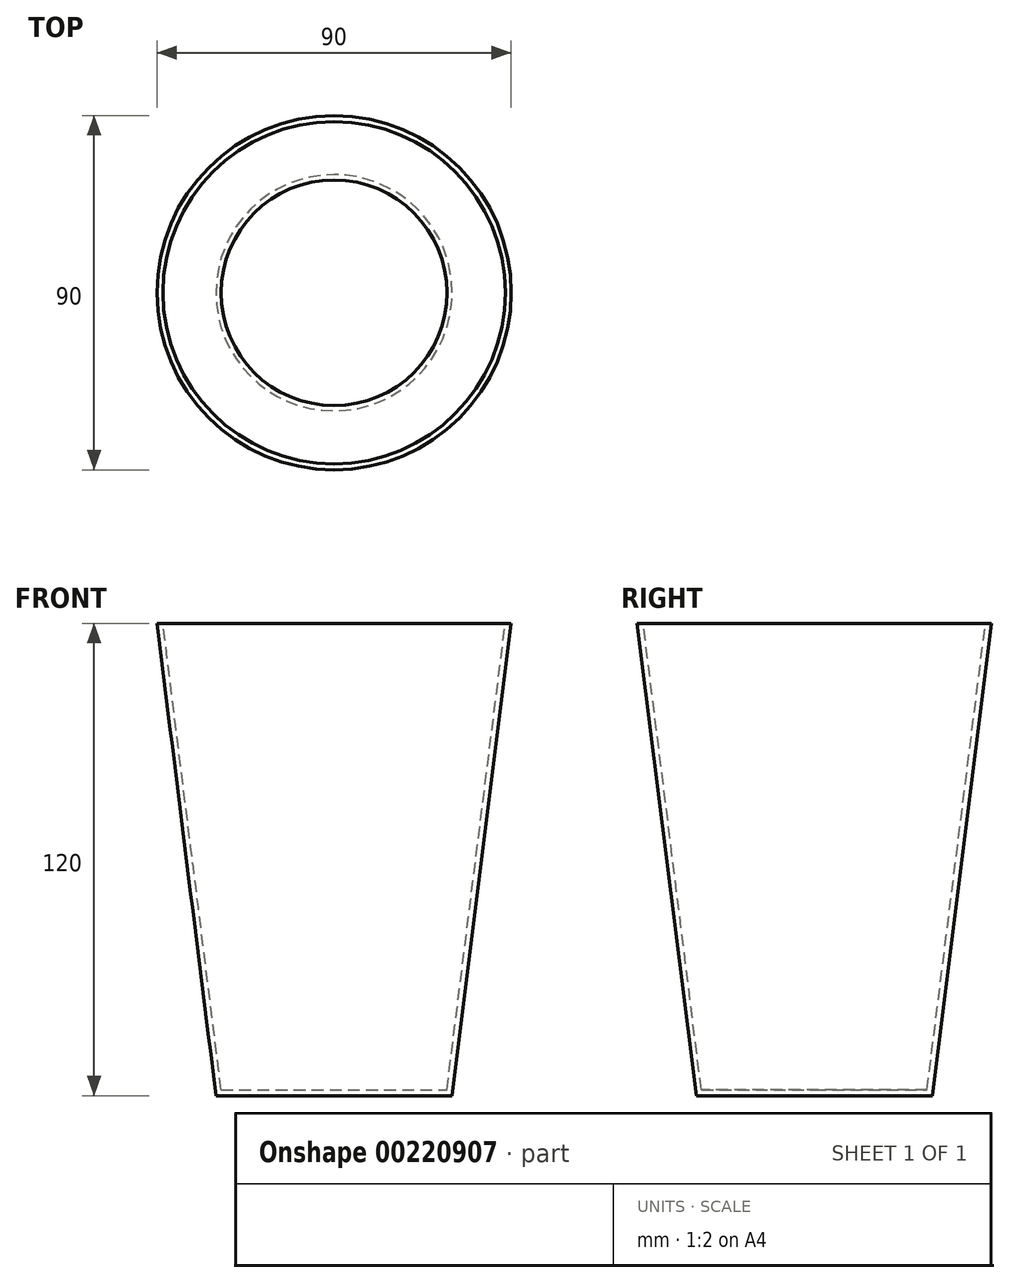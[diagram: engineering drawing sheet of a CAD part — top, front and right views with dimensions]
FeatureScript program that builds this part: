
annotation { "Feature Type Name" : "Feature", "Feature Type Description" : "" }
export const myFeature = defineFeature(function(context is Context, id is Id, definition is map)
    precondition{}
    {
        {
            var Q0;
            Q0=qCreatedBy(makeId("Top.planeOp"),FACE);
            var sketch = newSketch(context, id + "F0", { "sketchPlane" : qUnion([Q0])});
            skCircle(sketch, "E0", {"center": v(0, 0) * mm, "radius": 30 * mm});
            skSolve(sketch);
        }
        {
            var Q0;
            Q0=qCreatedBy(makeId("Front.planeOp"),FACE);
            var sketch = newSketch(context, id + "F1", { "sketchPlane" : qUnion([Q0])});
            skLineSegment(sketch, "E1", {"start": v(0, 0) * mm, "end": v(0, 120) * mm});
            skLineSegment(sketch, "E2", {"start": v(0, 0) * mm, "end": v(30, 0) * mm});
            skPoint(sketch, "E3.orphan", {"position": v(-30, 0) * mm});
            skLineSegment(sketch, "E4", {"start": v(30, 0) * mm, "end": v(45, 120) * mm});
            skLineSegment(sketch, "E5", {"start": v(0, 120) * mm, "end": v(45, 120) * mm});
            skSolve(sketch);
        }
        {
            var Q0;
            Q0=makeQuery(id+"F1.imprint","IMPRINT",FACE,{"disambiguationData":[TD([[makeQuery(id+"F1.imprint","IMPRINT",EDGE,{"derivedFrom":sQuery(id+"F1.wireOp",EDGE,"E1")}),-1.0]])]});
            var Q1;
            Q1=sQuery(id+"F0.wireOp",EDGE,"E0");
            revolve(context, id + "F2", {"entities" : qUnion([Q0]), "axis" : qUnion([Q1]), "revolveType" : RevolveType.FULL});
        }
        {
            var Q0;
            Q0=makeQuery(id+"F2.opRevolve","SWEPT_FACE",FACE,{"disambiguationData":[OSD([sQuery(id+"F1.wireOp",EDGE,"E5")])]});
            shell(context, id + "F3", {"entities" : qUnion([Q0]), "thickness" : 1.5 * mm});
        }
    });
